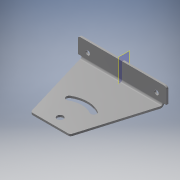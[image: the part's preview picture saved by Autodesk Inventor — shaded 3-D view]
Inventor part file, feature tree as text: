
AUTODESK INVENTOR PART (.ipt)
format: ipt  version: 2017 (Build 210142000, 142)  size: 248,320 bytes
history: native  units: mm
features: sheet_metal_op x6, other x6, sketch x3, plane x2, hole x1, mirror x1, chamfer x1
ambient origin geometry x8: Origin, YZ Plane, XZ Plane, XY Plane, X Axis, Y Axis, Z Axis, Center Point
bodies: Solid1 (feature_tree)
feature tree (20):
  sheet_metal_op  "Face1"
  sheet_metal_op  "Flange1"
  sheet_metal_op  "Flange2"
  hole  "Hole2"  [1 undecoded]
  plane  "Work Plane1"
  mirror  "Mirror1"
  chamfer  "Corner Round2"
  other  "A-Side Definition"
  sketch  "Sketch1"  dims[d2=165.0mm d3=80.0mm]
  other  "Plate1"
  other  "Plate2"
  sheet_metal_op  "Bend1"
  plane  "Work Plane2"
  sketch  "Sketch5"  dims[d4=146.0mm]
  sketch  "Sketch6"  dims[d5=42.5mm d6=3.9mm d23=0.0mm d24=0.0mm d25=4.0mm d26=2.0mm d27=8.0mm d28=3.9mm d29=36.0mm d30=90.0deg d31=3.9mm d68=20.0mm d69=20.0mm d34=9.0mm d35=6.0mm d36=4.0mm d37=2.0mm d38=90.0deg d39=4.0mm d40=20.594885mm d44=20.0mm d45=40.0mm d46=13.0mm d47=12.0mm d48=50.0mm d51=12.0mm d52=50.0mm d53=50.0mm d54=25.0mm d55=4.0mm d56=0.0mm d57=5.0mm d58=4.0mm d59=2.0mm d60=8.0mm d61=3.9mm d62=7.5mm d63=0.0mm d64=3.9mm d65=16.0mm d66=4.0mm d67=3.9mm d70=40.0mm d71=0.0mm d72=4.0mm d73=4.0mm]
  other  "Plate3"
  sheet_metal_op  "Bend2"
  sheet_metal_op  "Corner1"
  other  "Cut1"
  other  "Definition1"
note: 1 required parameter value undecoded (feature->parameter linkage not recoverable at this tier; creation-order binding heuristic only, values carry confidence <= 0.55)
